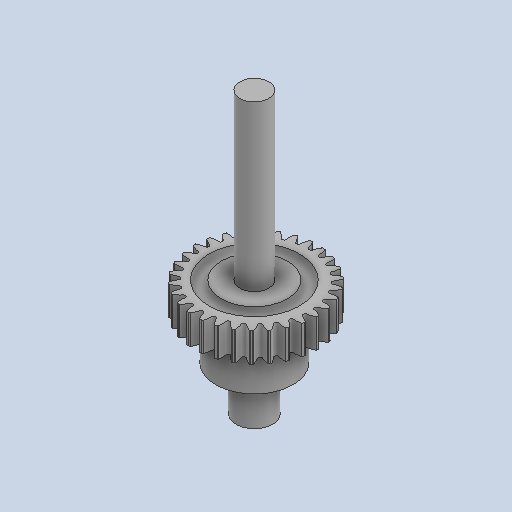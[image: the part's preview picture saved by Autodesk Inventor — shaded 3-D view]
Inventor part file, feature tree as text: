
AUTODESK INVENTOR PART (.ipt)
format: ipt  version: 2024 (Build 280153000, 153)  size: 742,912 bytes
history: native  units: mm
features: sketch x7, extrude x6, revolve x3, pattern_circular x2, fillet x1, other x1
ambient origin geometry x8: Origin, YZ Plane, XZ Plane, XY Plane, X Axis, Y Axis, Z Axis, Center Point
bodies: Body1 (feature_tree), Body2 (feature_tree)
feature tree (20):
  sketch  "Sketch4"  dims[d10=15.0mm d11=0.0mm d12=0.0mm d13=0.0mm]
  extrude  "Extrusion4"  TaperAngle=0.0deg  [1 undecoded]
  extrude  "Extrusion5"  Depth=15.0mm
  pattern_circular  "Circular Pattern1"  Count=4  [1 undecoded]
  extrude  "Extrusion6"  Depth=19.0mm
  extrude  "Extrusion7"  Depth=23.0mm
  extrude  "Extrusion8"  Depth=6.35mm
  fillet  "Fillet1"  Radius=20.0mm
  pattern_circular  "Circular Pattern2"  [2 undecoded]
  revolve  "Revolution1"  [1 undecoded]
  revolve  "Revolution2"  Angle=90.0deg
  revolve  "Revolution3"  [1 undecoded]
  sketch  "Sketch5"  dims[d14=300.0mm d15=360.0deg d17=15.0mm]
  sketch  "Sketch6"  dims[d18=85.071068mm d19=0.0mm d20=40.0mm]
  sketch  "Sketch7"  dims[d21=22.0mm d22=0.0mm d23=19.0mm]
  other  "Srf1"
  sketch  "Sketch8"  dims[d24=23.0mm d25=0.0mm d26=0.5mm]
  sketch  "Sketch10"  dims[d27=300.0mm d28=360.0deg d30=0.0mm d31=0.0mm d32=6.35mm d33=20.0mm]
  sketch  "Sketch11"  dims[d34=90.0deg d35=6.35mm d36=5.0mm d37=90.0deg d38=6.35mm d39=15.0mm d40=90.0deg d41=0.5mm d42=0.872665mm d43=0.5mm d44=0.872665mm]
  extrude  "ExtrusionSrf1"  Depth=15.0mm
note: 6 required parameter values undecoded (feature->parameter linkage not recoverable at this tier; creation-order binding heuristic only, values carry confidence <= 0.55)